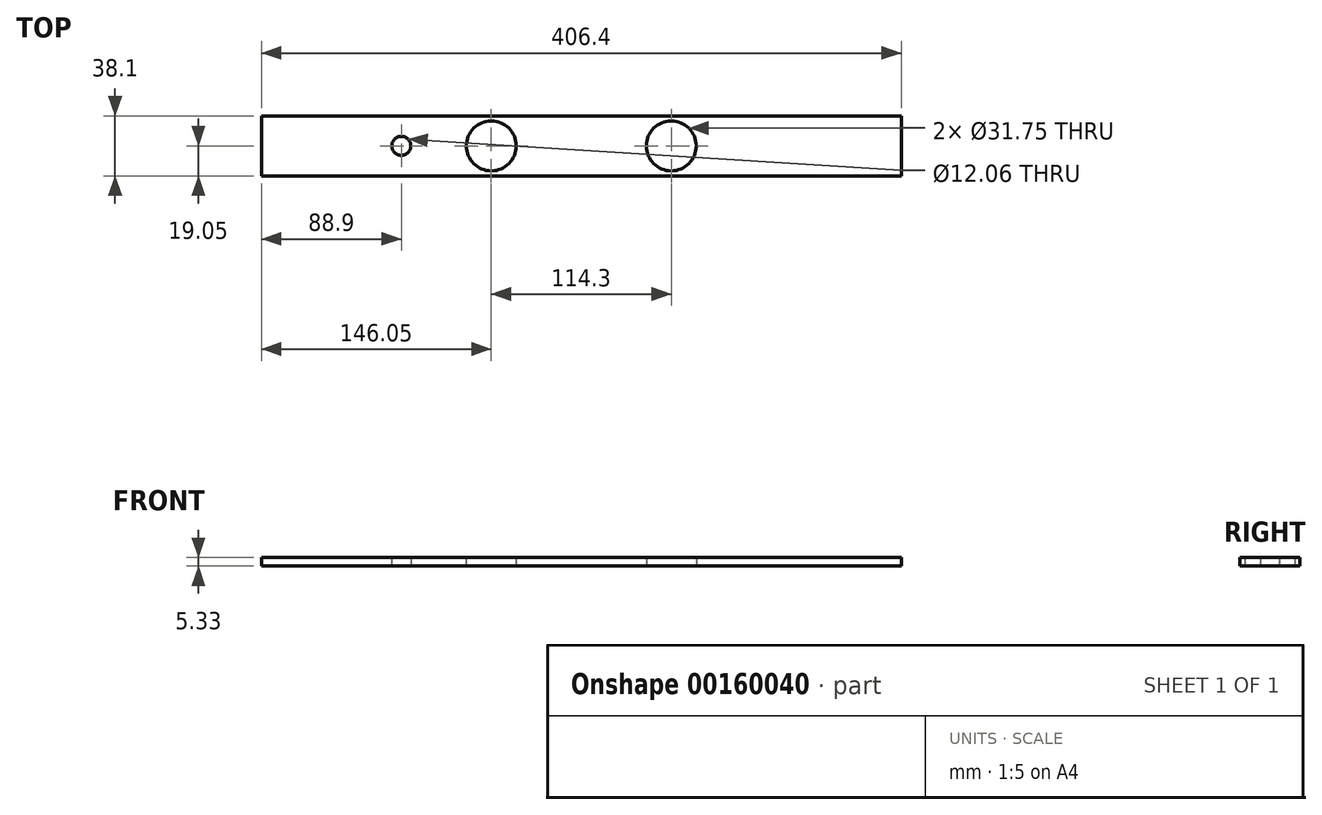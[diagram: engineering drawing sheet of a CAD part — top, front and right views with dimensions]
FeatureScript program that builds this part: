
annotation { "Feature Type Name" : "Feature", "Feature Type Description" : "" }
export const myFeature = defineFeature(function(context is Context, id is Id, definition is map)
    precondition{}
    {
        {
            var Q0;
            Q0=qCreatedBy(makeId("Top.planeOp"),FACE);
            var sketch = newSketch(context, id + "F0", { "sketchPlane" : qUnion([Q0])});
            skLineSegment(sketch, "E0.bottom", {"start": v(0, 0) * mm, "end": v(406.4, 0) * mm});
            skLineSegment(sketch, "E0.top", {"start": v(0, 38.1) * mm, "end": v(406.4, 38.1) * mm});
            skLineSegment(sketch, "E0.left", {"start": v(0, 0) * mm, "end": v(0, 38.1) * mm});
            skLineSegment(sketch, "E0.right", {"start": v(406.4, 0) * mm, "end": v(406.4, 38.1) * mm});
            skCircle(sketch, "E1", {"center": v(146.05, 19.05) * mm, "radius": 15.88 * mm});
            skCircle(sketch, "E2", {"center": v(88.9, 19.05) * mm, "radius": 6.03 * mm});
            skCircle(sketch, "E3", {"center": v(260.35, 19.05) * mm, "radius": 15.88 * mm});
            skSolve(sketch);
        }
        {
            var Q0;
            Q0 = qSketchRegion(id + "F0", true);
            extrude(context, id + "F1", {"entities" : qUnion([Q0]), "depth" : 5.33 * mm});
        }
    });
